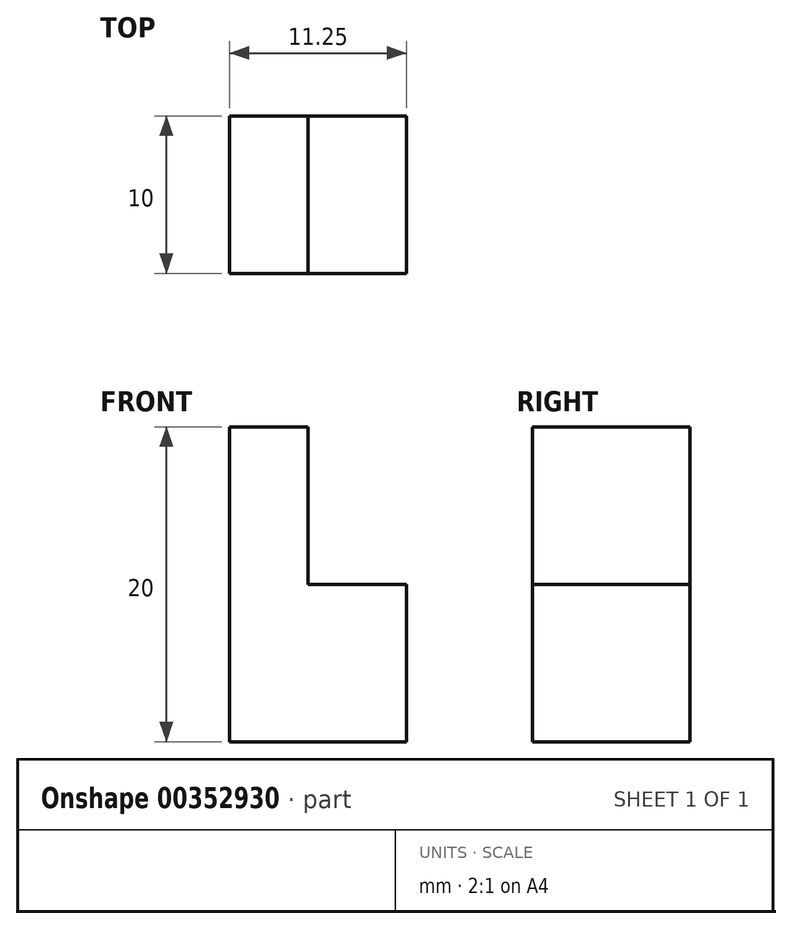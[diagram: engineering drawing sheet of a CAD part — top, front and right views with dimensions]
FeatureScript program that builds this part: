
annotation { "Feature Type Name" : "Feature", "Feature Type Description" : "" }
export const myFeature = defineFeature(function(context is Context, id is Id, definition is map)
    precondition{}
    {
        {
            var Q0;
            Q0=qCreatedBy(makeId("Front.planeOp"),FACE);
            var sketch = newSketch(context, id + "F0", { "sketchPlane" : qUnion([Q0])});
            skLineSegment(sketch, "E0", {"start": v(-11.25, 0) * mm, "end": v(-11.25, 9.97) * mm});
            skLineSegment(sketch, "E1", {"start": v(-11.25, 9.97) * mm, "end": v(-6.25, 9.97) * mm});
            skLineSegment(sketch, "E2", {"start": v(-6.25, 9.97) * mm, "end": v(-6.25, -0.03) * mm});
            skLineSegment(sketch, "E3", {"start": v(-6.25, -0.03) * mm, "end": v(0, -0.03) * mm});
            skLineSegment(sketch, "E4", {"start": v(0, -0.03) * mm, "end": v(0, -10.03) * mm});
            skLineSegment(sketch, "E5", {"start": v(0, -10.03) * mm, "end": v(-11.25, -10.03) * mm});
            skLineSegment(sketch, "E6", {"start": v(-11.25, -10.03) * mm, "end": v(-11.25, 0) * mm});
            skSolve(sketch);
        }
        {
            var Q0;
            Q0=makeQuery(id+"F0.imprint","IMPRINT",FACE,{"disambiguationData":[TD([[makeQuery(id+"F0.imprint","IMPRINT",EDGE,{"derivedFrom":sQuery(id+"F0.wireOp",EDGE,"E0")}),-1.0]])]});
            extrude(context, id + "F1", {"entities" : qUnion([Q0]), "depth" : 10 * mm});
        }
    });
